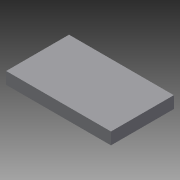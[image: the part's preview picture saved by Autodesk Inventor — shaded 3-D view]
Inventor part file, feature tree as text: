
AUTODESK INVENTOR PART (.ipt)
format: ipt  version: 2015 (Build 190159000, 159)  size: 68,096 bytes
history: native  units: in
note: dims shown in document units (in); Inventor stores cm internally (conversion verified against a paired STEP export)
features: extrude x1, sketch x1
ambient origin geometry x8: Origin, YZ Plane, XZ Plane, XY Plane, X Axis, Y Axis, Z Axis, Center Point
bodies: Solid1 (feature_tree)
feature tree (2):
  extrude  "Extrusion1"  Depth=0.8268in
  sketch  "Sketch1"  dims[d0=1.378in d1=0.8268in d2=0.1575in d3=0.0in]
